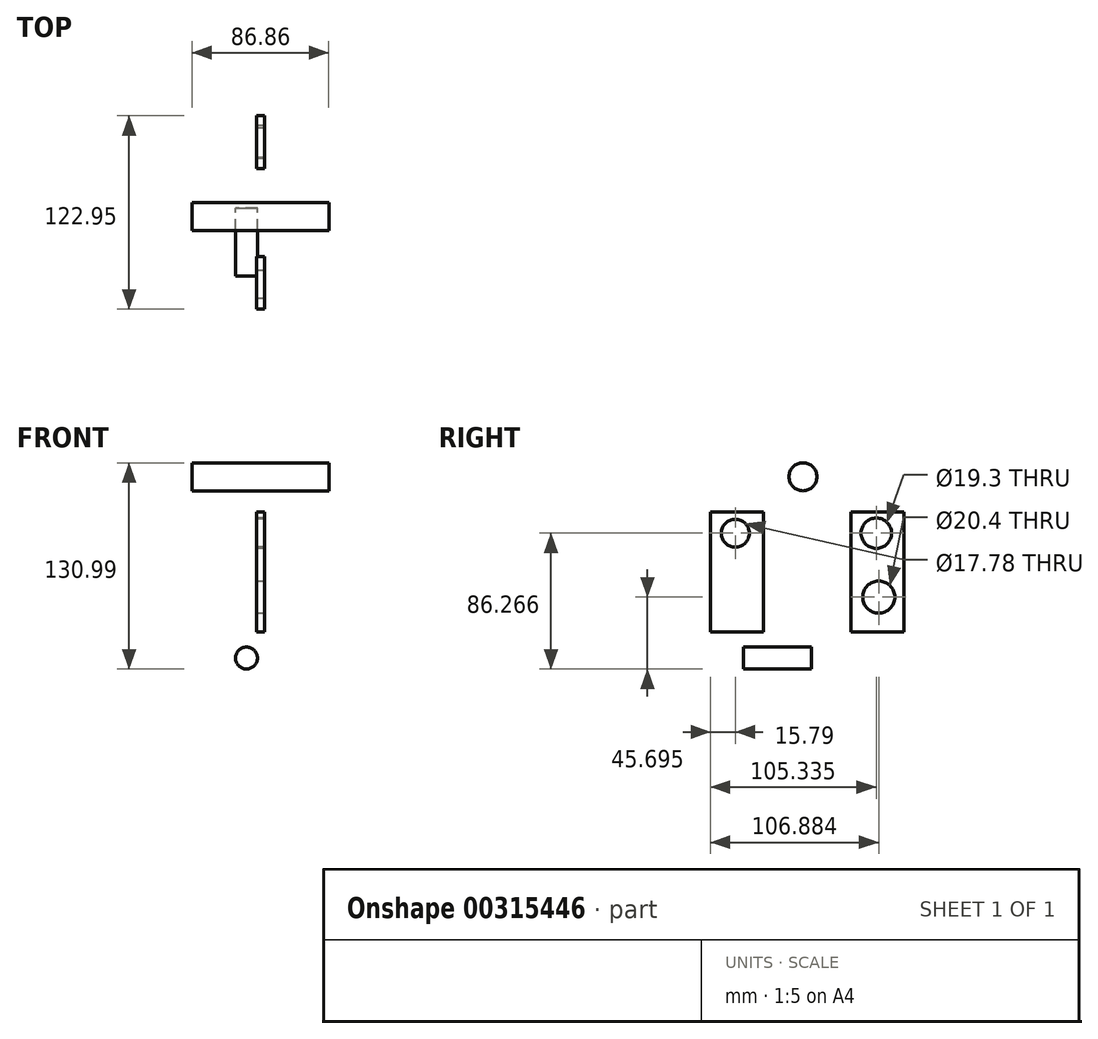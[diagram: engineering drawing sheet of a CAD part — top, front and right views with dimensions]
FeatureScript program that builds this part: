
annotation { "Feature Type Name" : "Feature", "Feature Type Description" : "" }
export const myFeature = defineFeature(function(context is Context, id is Id, definition is map)
    precondition{}
    {
        {
            var Q0;
            Q0=qCreatedBy(makeId("Right.planeOp"),FACE);
            var sketch = newSketch(context, id + "F0", { "sketchPlane" : qUnion([Q0])});
            skLineSegment(sketch, "E0.bottom", {"start": v(-64.15, 25.02) * mm, "end": v(-30.57, 25.02) * mm});
            skLineSegment(sketch, "E0.top", {"start": v(-64.15, -51.18) * mm, "end": v(-30.57, -51.18) * mm});
            skLineSegment(sketch, "E0.left", {"start": v(-64.15, 25.02) * mm, "end": v(-64.15, -51.18) * mm});
            skLineSegment(sketch, "E0.right", {"start": v(-30.57, 25.02) * mm, "end": v(-30.57, -51.18) * mm});
            skLineSegment(sketch, "E1.bottom", {"start": v(25.22, 25.23) * mm, "end": v(58.8, 25.23) * mm});
            skLineSegment(sketch, "E1.top", {"start": v(25.22, -50.97) * mm, "end": v(58.8, -50.97) * mm});
            skLineSegment(sketch, "E1.left", {"start": v(25.22, 25.23) * mm, "end": v(25.22, -50.97) * mm});
            skLineSegment(sketch, "E1.right", {"start": v(58.8, 25.23) * mm, "end": v(58.8, -50.97) * mm});
            skCircle(sketch, "E2", {"center": v(-5.39, 47.47) * mm, "radius": 8.9 * mm});
            skSolve(sketch);
        }
        {
            var Q0;
            Q0=makeQuery(id+"F0.imprint","IMPRINT",FACE,{"disambiguationData":[TD([[makeQuery(id+"F0.imprint","IMPRINT",EDGE,{"derivedFrom":sQuery(id+"F0.wireOp",EDGE,"E0.bottom")}),-1.0]])]});
            var Q1;
            Q1=makeQuery(id+"F0.imprint","IMPRINT",FACE,{"disambiguationData":[TD([[makeQuery(id+"F0.imprint","IMPRINT",EDGE,{"derivedFrom":sQuery(id+"F0.wireOp",EDGE,"E1.bottom")}),-1.0]])]});
            extrude(context, id + "F1", {"entities" : qUnion([Q0, Q1]), "endBound" : BoundingType.SYMMETRIC, "oppositeDirection" : true, "depth" : 5.08 * mm});
        }
        {
            var Q0;
            Q0=makeQuery(id+"F0.imprint","IMPRINT",FACE,{"disambiguationData":[TD([[makeQuery(id+"F0.imprint","IMPRINT",EDGE,{"derivedFrom":sQuery(id+"F0.wireOp",EDGE,"E2")}),1.0]])]});
            extrude(context, id + "F2", {"entities" : qUnion([Q0]), "endBound" : BoundingType.SYMMETRIC, "depth" : 86.87 * mm});
        }
        {
            var Q0;
            Q0=qCreatedBy(makeId("Right.planeOp"),FACE);
            var sketch = newSketch(context, id + "F3", { "sketchPlane" : qUnion([Q0])});
            skCircle(sketch, "E3", {"center": v(-48.36, 11.64) * mm, "radius": 8.9 * mm});
            skCircle(sketch, "E4", {"center": v(41.19, 11.64) * mm, "radius": 9.65 * mm});
            skSolve(sketch);
        }
        {
            var Q0;
            Q0 = qSketchRegion(id + "F3", true);
            extrude(context, id + "F4", {"entities" : qUnion([Q0]), "operationType" : NewBodyOperationType.REMOVE, "endBound" : BoundingType.SYMMETRIC, "depth" : 43.18 * mm});
        }
        {
            var Q0;
            Q0 = qSketchRegion(id + "F3", true);
            extrude(context, id + "F5", {"entities" : qUnion([Q0]), "operationType" : NewBodyOperationType.REMOVE, "endBound" : BoundingType.SYMMETRIC, "oppositeDirection" : true, "depth" : 25.4 * mm});
        }
        {
            var Q0;
            Q0=qCreatedBy(makeId("Right.planeOp"),FACE);
            var sketch = newSketch(context, id + "F6", { "sketchPlane" : qUnion([Q0])});
            skCircle(sketch, "E5", {"center": v(42.73, -28.94) * mm, "radius": 10.2 * mm});
            skSolve(sketch);
        }
        {
            var Q0;
            Q0 = qSketchRegion(id + "F6", true);
            extrude(context, id + "F7", {"entities" : qUnion([Q0]), "operationType" : NewBodyOperationType.REMOVE, "endBound" : BoundingType.SYMMETRIC, "oppositeDirection" : true, "depth" : 25.4 * mm});
        }
        {
            var Q0;
            Q0=qCreatedBy(makeId("Front.planeOp"),FACE);
            var sketch = newSketch(context, id + "F8", { "sketchPlane" : qUnion([Q0])});
            skCircle(sketch, "E6", {"center": v(-8.88, -67.67) * mm, "radius": 6.96 * mm});
            skSolve(sketch);
        }
        {
            var Q0;
            Q0 = qSketchRegion(id + "F8", true);
            extrude(context, id + "F9", {"entities" : qUnion([Q0]), "depth" : 43.18 * mm});
        }
    });
